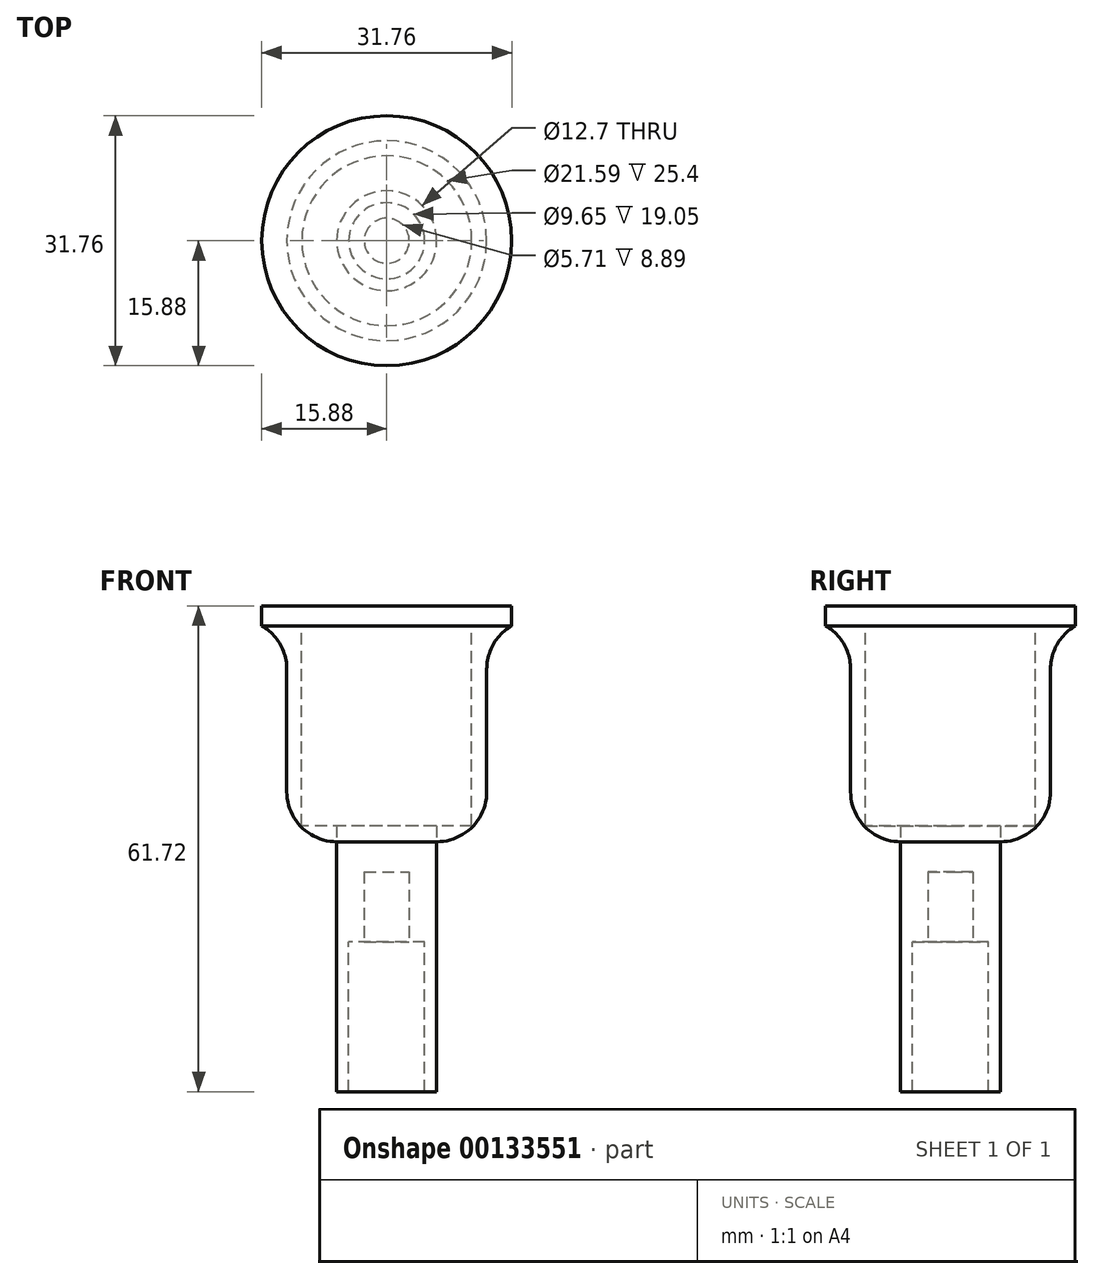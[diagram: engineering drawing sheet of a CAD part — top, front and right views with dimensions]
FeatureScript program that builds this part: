
annotation { "Feature Type Name" : "Feature", "Feature Type Description" : "" }
export const myFeature = defineFeature(function(context is Context, id is Id, definition is map)
    precondition{}
    {
        {
            var Q0;
            Q0=qCreatedBy(makeId("Top.planeOp"),FACE);
            var sketch = newSketch(context, id + "F0", { "sketchPlane" : qUnion([Q0])});
            skCircle(sketch, "E0", {"center": v(0, 0) * mm, "radius": 6.35 * mm});
            skSolve(sketch);
        }
        {
            var Q0;
            Q0 = qSketchRegion(id + "F0", true);
            extrude(context, id + "F1", {"entities" : qUnion([Q0]), "depth" : 19.05 * mm});
        }
        {
            var Q0;
            Q0=makeQuery(id+"F1.opExtrude","CAP_FACE",FACE,{"disambiguationData":[OSD([sQuery(id+"F0.wireOp",EDGE,"E0")])],"isStart":false});
            var sketch = newSketch(context, id + "F2", { "sketchPlane" : qUnion([Q0])});
            skCircle(sketch, "E1", {"center": v(0, 0) * mm, "radius": 4.83 * mm});
            skSolve(sketch);
        }
        {
            var Q0;
            Q0 = qSketchRegion(id + "F2", true);
            extrude(context, id + "F3", {"entities" : qUnion([Q0]), "operationType" : NewBodyOperationType.REMOVE, "endBound" : BoundingType.THROUGH_ALL, "oppositeDirection" : true, "depth" : 25.4 * mm});
        }
        {
            var Q0;
            Q0=makeQuery(id+"F1.opExtrude","CAP_FACE",FACE,{"disambiguationData":[OSD([sQuery(id+"F0.wireOp",EDGE,"E0")])],"isStart":false});
            var sketch = newSketch(context, id + "F4", { "sketchPlane" : qUnion([Q0])});
            skCircle(sketch, "E2", {"center": v(0, 0) * mm, "radius": 6.35 * mm});
            skSolve(sketch);
        }
        {
            var Q0;
            Q0 = qSketchRegion(id + "F4", true);
            extrude(context, id + "F5", {"entities" : qUnion([Q0]), "operationType" : NewBodyOperationType.ADD, "depth" : 12.7 * mm});
        }
        {
            var Q0;
            Q0=makeQuery(id+"F5.opExtrude","CAP_FACE",FACE,{"disambiguationData":[OSD([sQuery(id+"F4.wireOp",EDGE,"E2")])],"isStart":true});
            var sketch = newSketch(context, id + "F6", { "sketchPlane" : qUnion([Q0])});
            skCircle(sketch, "E3", {"center": v(0, 0) * mm, "radius": 2.86 * mm});
            skSolve(sketch);
        }
        {
            var Q0;
            Q0 = qSketchRegion(id + "F6", true);
            extrude(context, id + "F7", {"entities" : qUnion([Q0]), "operationType" : NewBodyOperationType.REMOVE, "oppositeDirection" : true, "depth" : 8.9 * mm});
        }
        {
            var Q0;
            Q0=makeQuery(id+"F5.opExtrude","CAP_FACE",FACE,{"disambiguationData":[OSD([sQuery(id+"F4.wireOp",EDGE,"E2")])],"isStart":false});
            var sketch = newSketch(context, id + "F8", { "sketchPlane" : qUnion([Q0])});
            skCircle(sketch, "E4", {"center": v(0, 0) * mm, "radius": 12.7 * mm});
            skSolve(sketch);
        }
        {
            var Q0;
            Q0=makeQuery(id+"F8.imprint","IMPRINT",FACE,{"disambiguationData":[TD([[makeQuery(id+"F8.imprint","IMPRINT",EDGE,{"derivedFrom":sQuery(id+"F8.wireOp",EDGE,"E4")}),1.0]])]});
            extrude(context, id + "F9", {"entities" : qUnion([Q0]), "depth" : 2.03 * mm});
        }
        {
            var Q0;
            Q0=makeQuery(id+"F9.opExtrude","CAP_FACE",FACE,{"disambiguationData":[OSD([sQuery(id+"F4.wireOp",EDGE,"E2"),sQuery(id+"F8.wireOp",EDGE,"E4")])],"isStart":false});
            var sketch = newSketch(context, id + "F10", { "sketchPlane" : qUnion([Q0])});
            skCircle(sketch, "E5", {"center": v(0, 0) * mm, "radius": 12.7 * mm});
            skSolve(sketch);
        }
        {
            var Q0;
            Q0 = qSketchRegion(id + "F10", true);
            extrude(context, id + "F11", {"entities" : qUnion([Q0]), "operationType" : NewBodyOperationType.ADD, "depth" : 25.4 * mm});
        }
        {
            var Q0;
            Q0=makeQuery(id+"F11.opExtrude","CAP_FACE",FACE,{"disambiguationData":[OSD([sQuery(id+"F10.wireOp",EDGE,"E5")])],"isStart":false});
            var sketch = newSketch(context, id + "F12", { "sketchPlane" : qUnion([Q0])});
            skCircle(sketch, "E6", {"center": v(0, 0) * mm, "radius": 10.8 * mm});
            skSolve(sketch);
        }
        {
            var Q0;
            Q0 = qSketchRegion(id + "F12", true);
            extrude(context, id + "F13", {"entities" : qUnion([Q0]), "operationType" : NewBodyOperationType.REMOVE, "oppositeDirection" : true, "depth" : 25.4 * mm});
        }
        {
            var Q0;
            Q0=makeQuery(id+"F11.opExtrude","CAP_FACE",FACE,{"disambiguationData":[OSD([sQuery(id+"F10.wireOp",EDGE,"E5")])],"isStart":false});
            var sketch = newSketch(context, id + "F14", { "sketchPlane" : qUnion([Q0])});
            skCircle(sketch, "E7", {"center": v(0, 0) * mm, "radius": 15.88 * mm});
            skSolve(sketch);
        }
        {
            var Q0;
            Q0 = qSketchRegion(id + "F14", true);
            extrude(context, id + "F15", {"entities" : qUnion([Q0]), "operationType" : NewBodyOperationType.ADD, "depth" : 2.54 * mm});
        }
        {
            var Q0;
            Q0=makeQuery(id+"F11.boolean.opBoolean","MERGE",FACE,{"derivedFrom":[makeQuery(id+"F9.opExtrude","SWEPT_FACE",FACE,{"disambiguationData":[OSD([sQuery(id+"F8.wireOp",EDGE,"E4")])]}),makeQuery(id+"F11.opExtrude","SWEPT_FACE",FACE,{"disambiguationData":[OSD([sQuery(id+"F10.wireOp",EDGE,"E5")])]})]});
            fillet(context, id + "F16", {"entities" : qUnion([Q0]), "radius" : 6.35 * mm, "tangentPropagation" : true, "allowEdgeOverflow" : false});
        }
    });
